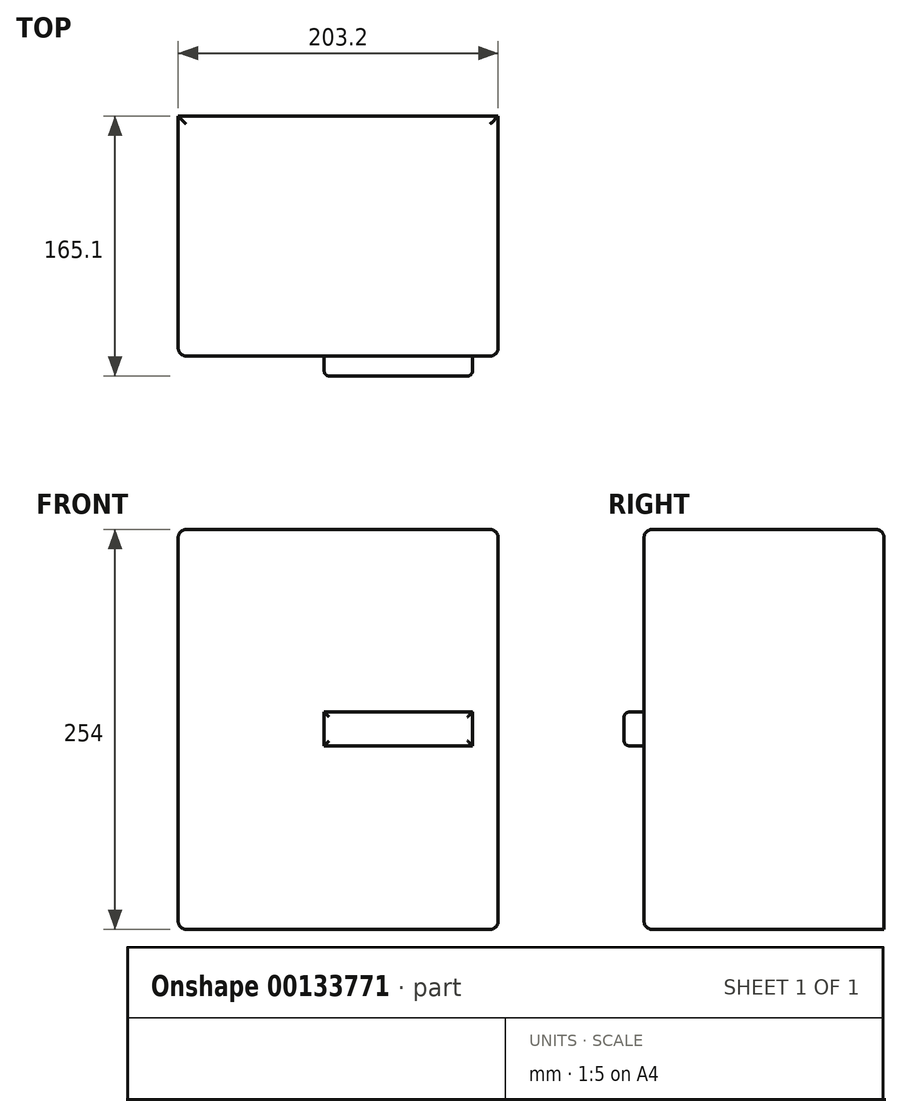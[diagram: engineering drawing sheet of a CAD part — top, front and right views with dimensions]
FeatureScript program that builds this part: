
annotation { "Feature Type Name" : "Feature", "Feature Type Description" : "" }
export const myFeature = defineFeature(function(context is Context, id is Id, definition is map)
    precondition{}
    {
        {
            var Q0;
            Q0=qCreatedBy(makeId("Front.planeOp"),FACE);
            var sketch = newSketch(context, id + "F0", { "sketchPlane" : qUnion([Q0])});
            skLineSegment(sketch, "E0.bottom", {"start": v(-171.88, 240.86) * mm, "end": v(31.32, 240.86) * mm});
            skLineSegment(sketch, "E0.top", {"start": v(-171.88, -13.14) * mm, "end": v(31.32, -13.14) * mm});
            skLineSegment(sketch, "E0.left", {"start": v(-171.88, 240.86) * mm, "end": v(-171.88, -13.14) * mm});
            skLineSegment(sketch, "E0.right", {"start": v(31.32, 240.86) * mm, "end": v(31.32, -13.14) * mm});
            skSolve(sketch);
        }
        {
            var Q0;
            Q0=makeQuery(id+"F0.imprint","IMPRINT",FACE,{"disambiguationData":[TD([[makeQuery(id+"F0.imprint","IMPRINT",EDGE,{"derivedFrom":sQuery(id+"F0.wireOp",EDGE,"E0.bottom")}),-1.0]])]});
            extrude(context, id + "F1", {"entities" : qUnion([Q0]), "depth" : 152.4 * mm});
        }
        {
            var Q0;
            Q0=makeQuery(id+"F1.opExtrude","CAP_EDGE",EDGE,{"disambiguationData":[OSD([sQuery(id+"F0.wireOp",EDGE,"E0.bottom")])],"isStart":false});
            var Q1;
            Q1=makeQuery(id+"F1.opExtrude","SWEPT_EDGE",EDGE,{"disambiguationData":[OSD([sQuery(id+"F0.wireOp",EDGE,"E0.bottom"),sQuery(id+"F0.wireOp",EDGE,"E0.right")])]});
            var Q2;
            Q2=makeQuery(id+"F1.opExtrude","SWEPT_EDGE",EDGE,{"disambiguationData":[OSD([sQuery(id+"F0.wireOp",EDGE,"E0.bottom"),sQuery(id+"F0.wireOp",EDGE,"E0.left")])]});
            var Q3;
            Q3=makeQuery(id+"F1.opExtrude","CAP_EDGE",EDGE,{"disambiguationData":[OSD([sQuery(id+"F0.wireOp",EDGE,"E0.bottom")])],"isStart":true});
            var Q4;
            Q4=makeQuery(id+"F1.opExtrude","CAP_EDGE",EDGE,{"disambiguationData":[OSD([sQuery(id+"F0.wireOp",EDGE,"E0.right")])],"isStart":false});
            var Q5;
            Q5=makeQuery(id+"F1.opExtrude","CAP_EDGE",EDGE,{"disambiguationData":[OSD([sQuery(id+"F0.wireOp",EDGE,"E0.left")])],"isStart":false});
            var Q6;
            Q6=makeQuery(id+"F1.opExtrude","CAP_EDGE",EDGE,{"disambiguationData":[OSD([sQuery(id+"F0.wireOp",EDGE,"E0.top")])],"isStart":false});
            var Q7;
            Q7=makeQuery(id+"F1.opExtrude","SWEPT_EDGE",EDGE,{"disambiguationData":[OSD([sQuery(id+"F0.wireOp",EDGE,"E0.top"),sQuery(id+"F0.wireOp",EDGE,"E0.right")])]});
            var Q8;
            Q8=makeQuery(id+"F1.opExtrude","SWEPT_EDGE",EDGE,{"disambiguationData":[OSD([sQuery(id+"F0.wireOp",EDGE,"E0.top"),sQuery(id+"F0.wireOp",EDGE,"E0.left")])]});
            fillet(context, id + "F2", {"entities" : qUnion([Q0, Q1, Q2, Q3, Q4, Q5, Q6, Q7, Q8]), "radius" : 5.08 * mm, "tangentPropagation" : true, "allowEdgeOverflow" : false});
        }
        {
            var Q0;
            Q0=makeQuery(id+"F1.opExtrude","CAP_FACE",FACE,{"disambiguationData":[OSD([sQuery(id+"F0.wireOp",EDGE,"E0.bottom"),sQuery(id+"F0.wireOp",EDGE,"E0.top"),sQuery(id+"F0.wireOp",EDGE,"E0.left"),sQuery(id+"F0.wireOp",EDGE,"E0.right")])],"isStart":false});
            var sketch = newSketch(context, id + "F3", { "sketchPlane" : qUnion([Q0])});
            skLineSegment(sketch, "E1.bottom", {"start": v(15.02, 103.5) * mm, "end": v(-79.14, 103.5) * mm});
            skLineSegment(sketch, "E1.top", {"start": v(15.02, 124.87) * mm, "end": v(-79.14, 124.87) * mm});
            skLineSegment(sketch, "E1.left", {"start": v(15.02, 103.5) * mm, "end": v(15.02, 124.87) * mm});
            skLineSegment(sketch, "E1.right", {"start": v(-79.14, 103.5) * mm, "end": v(-79.14, 124.87) * mm});
            skPoint(sketch, "E1.middle", {"position": v(-32.06, 114.19) * mm});
            skSolve(sketch);
        }
        {
            var Q0;
            Q0=makeQuery(id+"F3.imprint","IMPRINT",FACE,{"disambiguationData":[TD([[makeQuery(id+"F3.imprint","IMPRINT",EDGE,{"derivedFrom":sQuery(id+"F3.wireOp",EDGE,"E1.bottom")}),-1.0]])]});
            extrude(context, id + "F4", {"entities" : qUnion([Q0]), "operationType" : NewBodyOperationType.ADD, "depth" : 12.7 * mm});
        }
        {
            var Q0;
            Q0=makeQuery(id+"F4.opExtrude","CAP_FACE",FACE,{"disambiguationData":[OSD([sQuery(id+"F3.wireOp",EDGE,"E1.bottom"),sQuery(id+"F3.wireOp",EDGE,"E1.top"),sQuery(id+"F3.wireOp",EDGE,"E1.left"),sQuery(id+"F3.wireOp",EDGE,"E1.right")])],"isStart":false});
            var Q1;
            Q1=makeQuery(id+"F4.opExtrude","CAP_EDGE",EDGE,{"disambiguationData":[OSD([sQuery(id+"F3.wireOp",EDGE,"E1.top")])],"isStart":false});
            var Q2;
            Q2=makeQuery(id+"F4.opExtrude","CAP_EDGE",EDGE,{"disambiguationData":[OSD([sQuery(id+"F3.wireOp",EDGE,"E1.bottom")])],"isStart":false});
            var Q3;
            Q3=makeQuery(id+"F4.opExtrude","CAP_EDGE",EDGE,{"disambiguationData":[OSD([sQuery(id+"F3.wireOp",EDGE,"E1.right")])],"isStart":false});
            fillet(context, id + "F5", {"entities" : qUnion([Q0, Q1, Q2, Q3]), "radius" : 3.17 * mm, "tangentPropagation" : true, "allowEdgeOverflow" : false});
        }
    });
